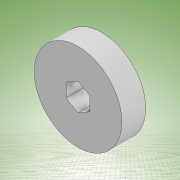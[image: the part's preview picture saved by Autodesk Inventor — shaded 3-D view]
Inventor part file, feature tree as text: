
AUTODESK INVENTOR PART (.ipt)
format: ipt  version: 2022 (Build 260153000, 153)  size: 118,784 bytes
history: native  units: mm
features: extrude x1, sketch x1
ambient origin geometry x8: Origin, YZ Plane, XZ Plane, XY Plane, X Axis, Y Axis, Z Axis, Center Point
bodies: Body1 (feature_tree)
feature tree (2):
  extrude  "Extrusión4"  Depth=6.0mm
  sketch  "Boceto4"  dims[d9=22.0mm d10=6.0mm d11=6.0mm d12=0.0mm]
